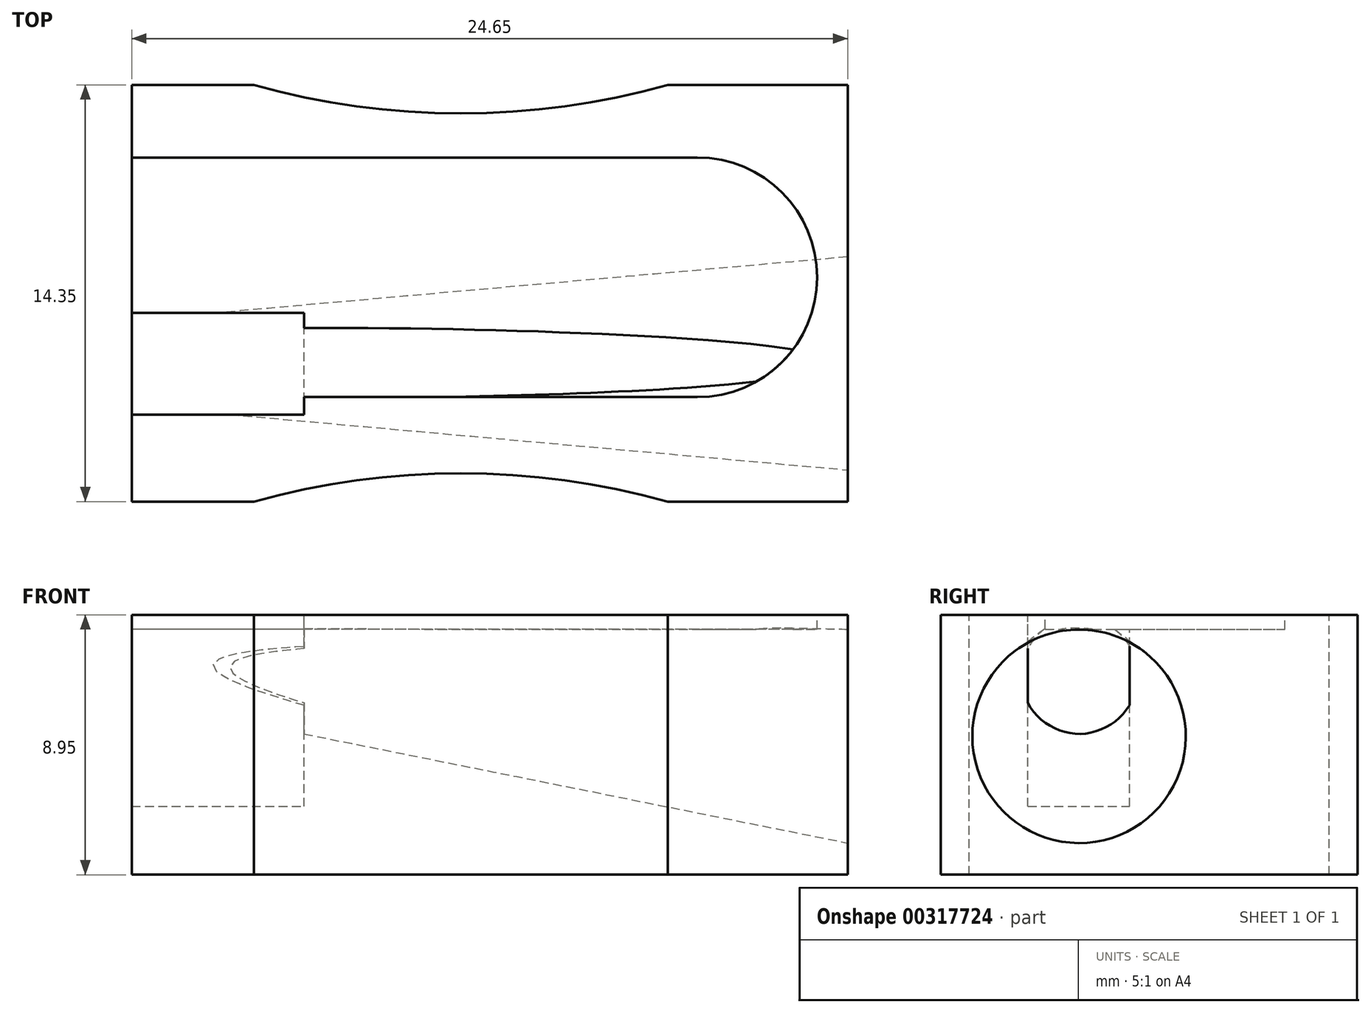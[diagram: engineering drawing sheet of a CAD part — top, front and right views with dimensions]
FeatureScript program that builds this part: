
annotation { "Feature Type Name" : "Feature", "Feature Type Description" : "" }
export const myFeature = defineFeature(function(context is Context, id is Id, definition is map)
    precondition{}
    {
        {
            var Q0;
            Q0=qCreatedBy(makeId("Front.planeOp"),FACE);
            var sketch = newSketch(context, id + "F0", { "sketchPlane" : qUnion([Q0])});
            skLineSegment(sketch, "E0.bottom", {"start": v(-23.85, 41.33) * mm, "end": v(0.8, 41.33) * mm});
            skLineSegment(sketch, "E0.top", {"start": v(-23.85, 32.38) * mm, "end": v(0.8, 32.38) * mm});
            skLineSegment(sketch, "E0.left", {"start": v(-23.85, 41.33) * mm, "end": v(-23.85, 32.38) * mm});
            skLineSegment(sketch, "E0.right", {"start": v(0.8, 41.33) * mm, "end": v(0.8, 32.38) * mm});
            skSolve(sketch);
        }
        {
            var Q0;
            Q0=makeQuery(id+"F0.imprint","IMPRINT",FACE,{"disambiguationData":[TD([[makeQuery(id+"F0.imprint","IMPRINT",EDGE,{"derivedFrom":sQuery(id+"F0.wireOp",EDGE,"E0.bottom")}),-1.0]])]});
            extrude(context, id + "F1", {"entities" : qUnion([Q0]), "depth" : 14.35 * mm});
        }
        {
            var Q0;
            Q0=makeQuery(id+"F1.opExtrude","SWEPT_FACE",FACE,{"disambiguationData":[OSD([sQuery(id+"F0.wireOp",EDGE,"E0.right")])]});
            var sketch = newSketch(context, id + "F2", { "sketchPlane" : qUnion([Q0])});
            skCircle(sketch, "E1", {"center": v(-9.58, 37.15) * mm, "radius": 3.67 * mm});
            skLineSegment(sketch, "E2", {"start": v(-9.58, 37.15) * mm, "end": v(-9.58, 40.82) * mm});
            skSolve(sketch);
        }
        {
            var Q0;
            Q0=makeQuery(id+"F1.opExtrude","SWEPT_FACE",FACE,{"disambiguationData":[OSD([sQuery(id+"F0.wireOp",EDGE,"E0.bottom")])]});
            var sketch = newSketch(context, id + "F3", { "sketchPlane" : qUnion([Q0])});
            skArc(sketch, "E3", {"start": v(-4.38, -10.75) * mm, "mid": v(-0.25, -6.63) * mm, "end": v(-4.38, -2.5) * mm});
            skLineSegment(sketch, "E4", {"start": v(-4.38, -2.5) * mm, "end": v(-23.85, -2.5) * mm});
            skLineSegment(sketch, "E5", {"start": v(-4.38, -10.75) * mm, "end": v(-17.91, -10.75) * mm});
            skLineSegment(sketch, "E6", {"start": v(-23.85, -11.35) * mm, "end": v(-17.91, -11.35) * mm});
            skLineSegment(sketch, "E7", {"start": v(-17.91, -11.35) * mm, "end": v(-17.91, -10.75) * mm});
            skSolve(sketch);
        }
        {
            var Q0;
            Q0=makeQuery(id+"F3.imprint","IMPRINT",FACE,{"disambiguationData":[TD([[makeQuery(id+"F3.imprint","IMPRINT",EDGE,{"derivedFrom":sQuery(id+"F3.wireOp",EDGE,"E3")}),1.0]])]});
            extrude(context, id + "F4", {"entities" : qUnion([Q0]), "operationType" : NewBodyOperationType.REMOVE, "oppositeDirection" : true, "depth" : 0.5 * mm});
        }
        {
            var Q0;
            Q0=makeQuery(id+"F1.opExtrude","SWEPT_FACE",FACE,{"disambiguationData":[OSD([sQuery(id+"F0.wireOp",EDGE,"E0.left")])]});
            var sketch = newSketch(context, id + "F5", { "sketchPlane" : qUnion([Q0])});
            skCircle(sketch, "E8", {"center": v(9.57, 39.9) * mm, "radius": 1.47 * mm});
            skLineSegment(sketch, "E9", {"start": v(9.57, 39.9) * mm, "end": v(9.57, 41.37) * mm});
            skSolve(sketch);
        }
        {
            var Q0;
            Q0=makeQuery(id+"F1.opExtrude","SWEPT_FACE",FACE,{"disambiguationData":[OSD([sQuery(id+"F0.wireOp",EDGE,"E0.bottom")])]});
            var sketch = newSketch(context, id + "F6", { "sketchPlane" : qUnion([Q0])});
            skArc(sketch, "E10", {"start": v(-5.4, -14.35) * mm, "mid": v(-12.52, -13.37) * mm, "end": v(-19.65, -14.35) * mm});
            skArc(sketch, "E11", {"start": v(-19.65, 0) * mm, "mid": v(-12.52, -0.98) * mm, "end": v(-5.4, 0) * mm});
            skArc(sketch, "E12", {"start": v(-18.08, -0.39) * mm, "mid": v(-17.6, -0.86) * mm, "end": v(-16.98, -0.6) * mm});
            skArc(sketch, "E13", {"start": v(-16.26, -0.71) * mm, "mid": v(-15.73, -1.3) * mm, "end": v(-15.07, -0.85) * mm});
            skArc(sketch, "E14", {"start": v(-14.22, -0.92) * mm, "mid": v(-13.65, -1.44) * mm, "end": v(-13.04, -0.97) * mm});
            skArc(sketch, "E15", {"start": v(-11.8, -0.97) * mm, "mid": v(-11.17, -1.47) * mm, "end": v(-10.6, -0.9) * mm});
            skArc(sketch, "E16", {"start": v(-9.67, -0.82) * mm, "mid": v(-9.01, -1.27) * mm, "end": v(-8.5, -0.67) * mm});
            skSolve(sketch);
        }
        {
            var Q0;
            {var subQ0=sQuery(id+"F6.wireOp",EDGE,"E10");Q0=makeQuery(id+"F6.imprint","IMPRINT",FACE,{"disambiguationData":[TD([[makeQuery(id+"F6.imprint","IMPRINT",EDGE,{"derivedFrom":subQ0}),1.0]])]});}
            var Q1;
            {var subQ0=sQuery(id+"F6.wireOp",EDGE,"E11");Q1=makeQuery(id+"F6.imprint","IMPRINT",FACE,{"disambiguationData":[TD([[makeQuery(id+"F6.imprint","IMPRINT",EDGE,{"derivedFrom":subQ0}),1.0]])]});}
            extrude(context, id + "F7", {"entities" : qUnion([Q0, Q1]), "operationType" : NewBodyOperationType.REMOVE, "oppositeDirection" : true, "depth" : 14.35 * mm});
        }
        {
            var Q0;
            Q0=makeQuery(id+"F4.boolean.opBoolean","COPY",FACE,{"derivedFrom":makeQuery(id+"F4.opExtrude","CAP_FACE",FACE,{"disambiguationData":[OSD([sQuery(id+"F0.wireOp",EDGE,"E0.bottom"),sQuery(id+"F0.wireOp",EDGE,"E0.left"),sQuery(id+"F3.wireOp",EDGE,"E3"),sQuery(id+"F3.wireOp",EDGE,"E4"),sQuery(id+"F3.wireOp",EDGE,"E5"),sQuery(id+"F3.wireOp",EDGE,"E6"),sQuery(id+"F3.wireOp",EDGE,"E7")])],"isStart":false})});
            var sketch = newSketch(context, id + "F8", { "sketchPlane" : qUnion([Q0])});
            skLineSegment(sketch, "E17.bottom", {"start": v(-17.91, -11.35) * mm, "end": v(-23.85, -11.35) * mm});
            skLineSegment(sketch, "E17.top", {"start": v(-17.91, -7.85) * mm, "end": v(-23.85, -7.85) * mm});
            skLineSegment(sketch, "E17.left", {"start": v(-17.91, -11.35) * mm, "end": v(-17.91, -7.85) * mm});
            skLineSegment(sketch, "E17.right", {"start": v(-23.85, -11.35) * mm, "end": v(-23.85, -7.85) * mm});
            skSolve(sketch);
        }
        {
            var Q0;
            {var subQ2=sQuery(id+"F8.wireOp",EDGE,"E17.bottom");Q0=makeQuery(id+"F8.imprint","IMPRINT",FACE,{"disambiguationData":[TD([[makeQuery(id+"F8.imprint","IMPRINT",EDGE,{"derivedFrom":subQ2}),1.0]])]});}
            extrude(context, id + "F9", {"entities" : qUnion([Q0]), "operationType" : NewBodyOperationType.REMOVE, "oppositeDirection" : true, "depth" : 6.1 * mm});
        }
        {
            var Q1;
            Q1 = qSketchRegion(id + "F5", true);
            var Q2;
            Q2 = qSketchRegion(id + "F2", true);
            loft(context, id + "F10", {"operationType" : NewBodyOperationType.REMOVE, "sheetProfilesArray" : [{ "sheetProfileEntities" : qUnion([Q1]) }, { "sheetProfileEntities" : qUnion([Q2]) }]});
        }
    });
